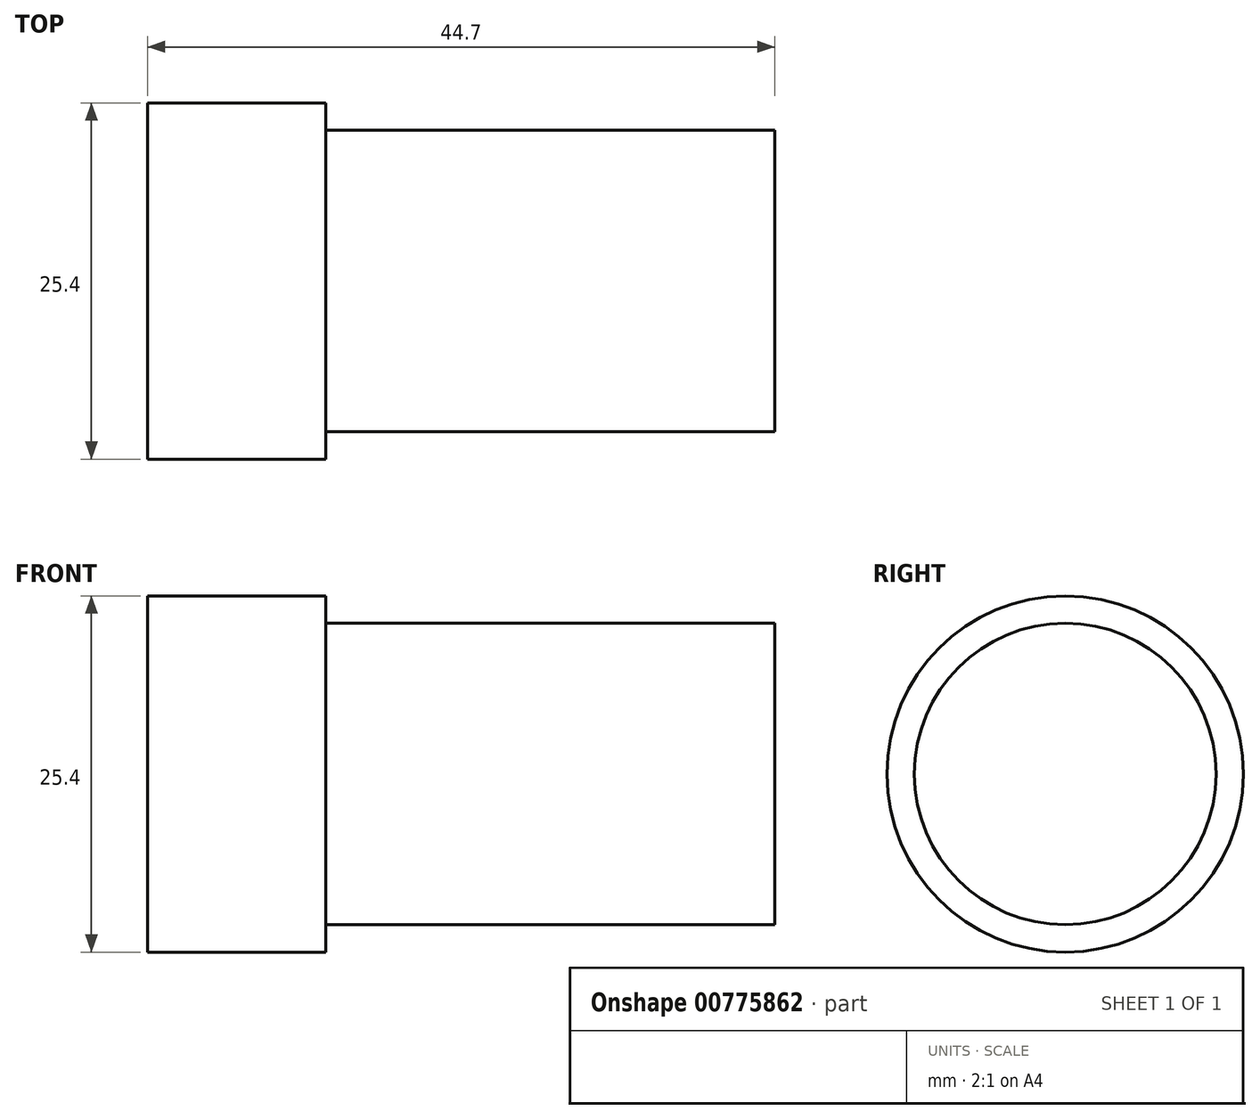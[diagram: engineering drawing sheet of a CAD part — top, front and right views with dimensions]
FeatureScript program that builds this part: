
annotation { "Feature Type Name" : "Feature", "Feature Type Description" : "" }
export const myFeature = defineFeature(function(context is Context, id is Id, definition is map)
    precondition{}
    {
        {
            var Q0;
            Q0=qCreatedBy(makeId("Front.planeOp"),FACE);
            var sketch = newSketch(context, id + "F0", { "sketchPlane" : qUnion([Q0])});
            skLineSegment(sketch, "E0.bottom", {"start": v(0, 0) * mm, "end": v(12.7, 0) * mm});
            skLineSegment(sketch, "E0.top", {"start": v(0, 12.7) * mm, "end": v(12.7, 12.7) * mm});
            skLineSegment(sketch, "E0.left", {"start": v(0, 0) * mm, "end": v(0, 12.7) * mm});
            skLineSegment(sketch, "E0.right", {"start": v(12.7, 0) * mm, "end": v(12.7, 12.7) * mm});
            skLineSegment(sketch, "E1.bottom", {"start": v(12.7, 0) * mm, "end": v(44.7, 0) * mm});
            skLineSegment(sketch, "E1.top", {"start": v(12.7, 10.75) * mm, "end": v(44.7, 10.75) * mm});
            skLineSegment(sketch, "E1.left", {"start": v(12.7, 0) * mm, "end": v(12.7, 10.75) * mm});
            skLineSegment(sketch, "E1.right", {"start": v(44.7, 0) * mm, "end": v(44.7, 10.75) * mm});
            skSolve(sketch);
        }
        {
            var Q0;
            Q0 = qSketchRegion(id + "F0", true);
            var Q1;
            Q1=sQuery(id+"F0.wireOp",EDGE,"E1.bottom");
            revolve(context, id + "F1", {"surfaceOperationType" : NewSurfaceOperationType.NEW, "entities" : qUnion([Q0]), "axis" : qUnion([Q1]), "revolveType" : RevolveType.FULL});
        }
    });
